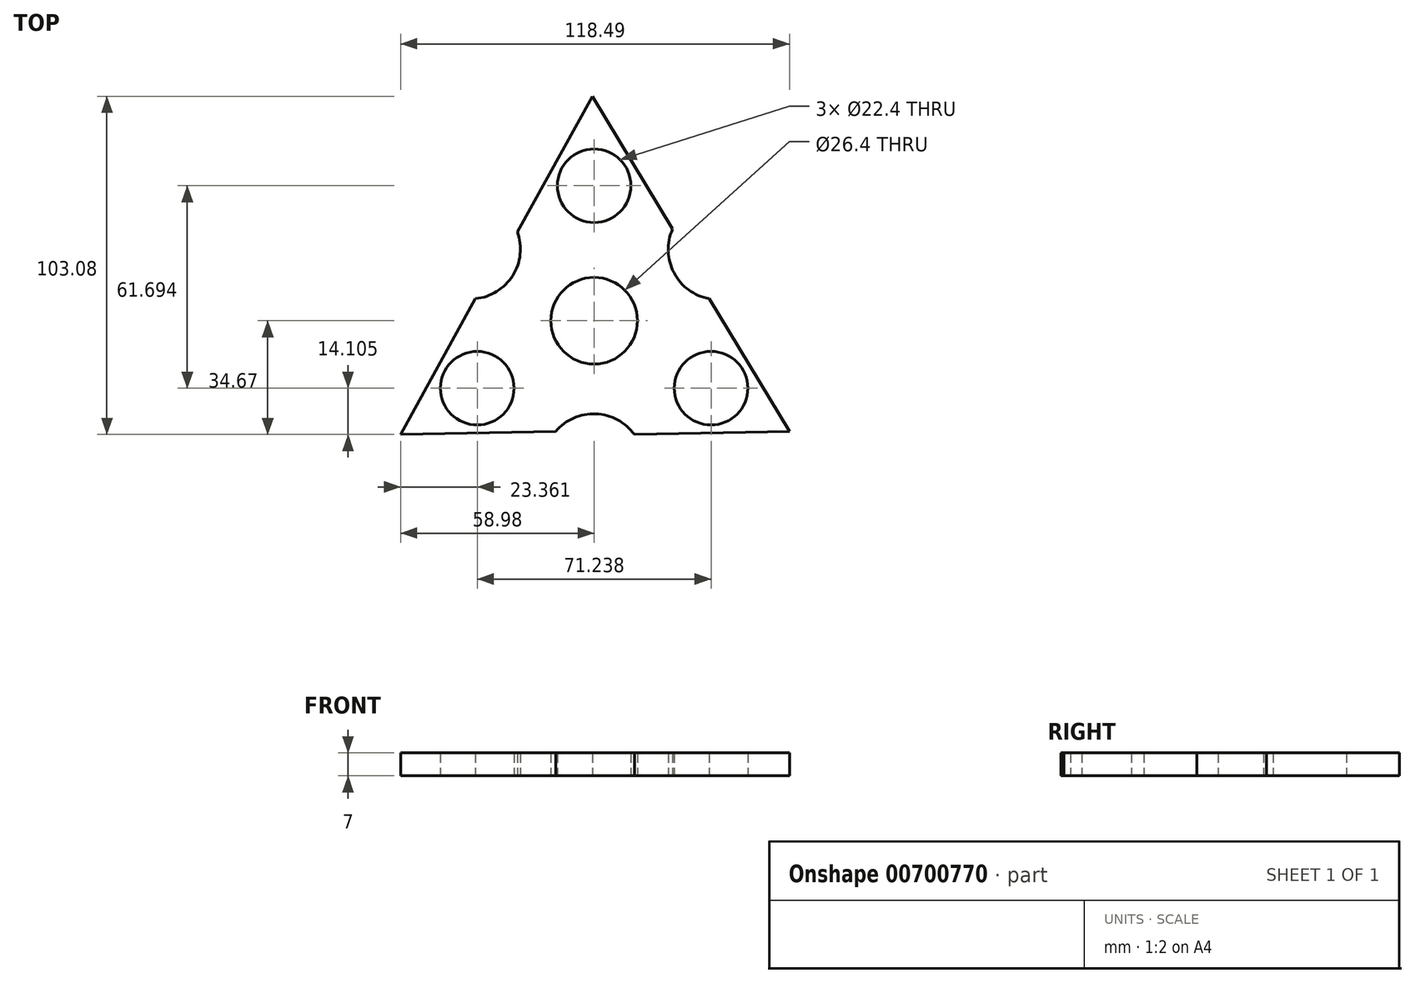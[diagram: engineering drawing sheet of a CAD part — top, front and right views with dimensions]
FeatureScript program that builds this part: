
annotation { "Feature Type Name" : "Feature", "Feature Type Description" : "" }
export const myFeature = defineFeature(function(context is Context, id is Id, definition is map)
    precondition{}
    {
        {
            var Q0;
            Q0=qCreatedBy(makeId("Top.planeOp"),FACE);
            var sketch = newSketch(context, id + "F0", { "sketchPlane" : qUnion([Q0])});
            skCircle(sketch, "E0", {"center": v(0, 0) * mm, "radius": 11.2 * mm});
            skCircle(sketch, "E1", {"center": v(0, 0) * mm, "radius": 13.2 * mm});
            skCircle(sketch, "E2", {"center": v(0, 41.13) * mm, "radius": 11.2 * mm});
            skLineSegment(sketch, "E3.0", {"start": v(-0.53, 68.41) * mm, "end": v(23.9, 27.95) * mm});
            skLineSegment(sketch, "E3.2", {"start": v(-23.36, 27.03) * mm, "end": v(-0.53, 68.41) * mm});
            skPoint(sketch, "E3.0.midPoint", {"position": v(11.68, 48.18) * mm});
            skLineSegment(sketch, "E4.1.0", {"start": v(-11.72, -33.74) * mm, "end": v(-58.98, -34.67) * mm});
            skLineSegment(sketch, "E4.1.1", {"start": v(-58.98, -34.67) * mm, "end": v(-36.15, 6.72) * mm});
            skCircle(sketch, "E4.1.4", {"center": v(-35.62, -20.56) * mm, "radius": 11.2 * mm});
            skLineSegment(sketch, "E4.2.0", {"start": v(35.09, 6.72) * mm, "end": v(59.51, -33.74) * mm});
            skLineSegment(sketch, "E4.2.1", {"start": v(59.51, -33.74) * mm, "end": v(12.26, -34.67) * mm});
            skCircle(sketch, "E4.2.4", {"center": v(35.62, -20.56) * mm, "radius": 11.2 * mm});
            skArc(sketch, "E5", {"start": v(-36.15, 6.72) * mm, "mid": v(-24.8, 13.76) * mm, "end": v(-23.36, 27.03) * mm});
            skArc(sketch, "E6.1.0", {"start": v(12.26, -34.67) * mm, "mid": v(0.5, -28.36) * mm, "end": v(-11.72, -33.74) * mm});
            skArc(sketch, "E6.2.0", {"start": v(23.9, 27.95) * mm, "mid": v(24.32, 14.6) * mm, "end": v(35.09, 6.72) * mm});
            skSolve(sketch);
        }
        {
            var Q0;
            Q0=makeQuery(id+"F0.imprint","IMPRINT",FACE,{"disambiguationData":[TD([[makeQuery(id+"F0.imprint","IMPRINT",EDGE,{"derivedFrom":sQuery(id+"F0.wireOp",EDGE,"E1")}),-1.0]])]});
            extrude(context, id + "F1", {"entities" : qUnion([Q0]), "depth" : 7 * mm, "offsetDistance" : 25 * mm});
        }
    });
